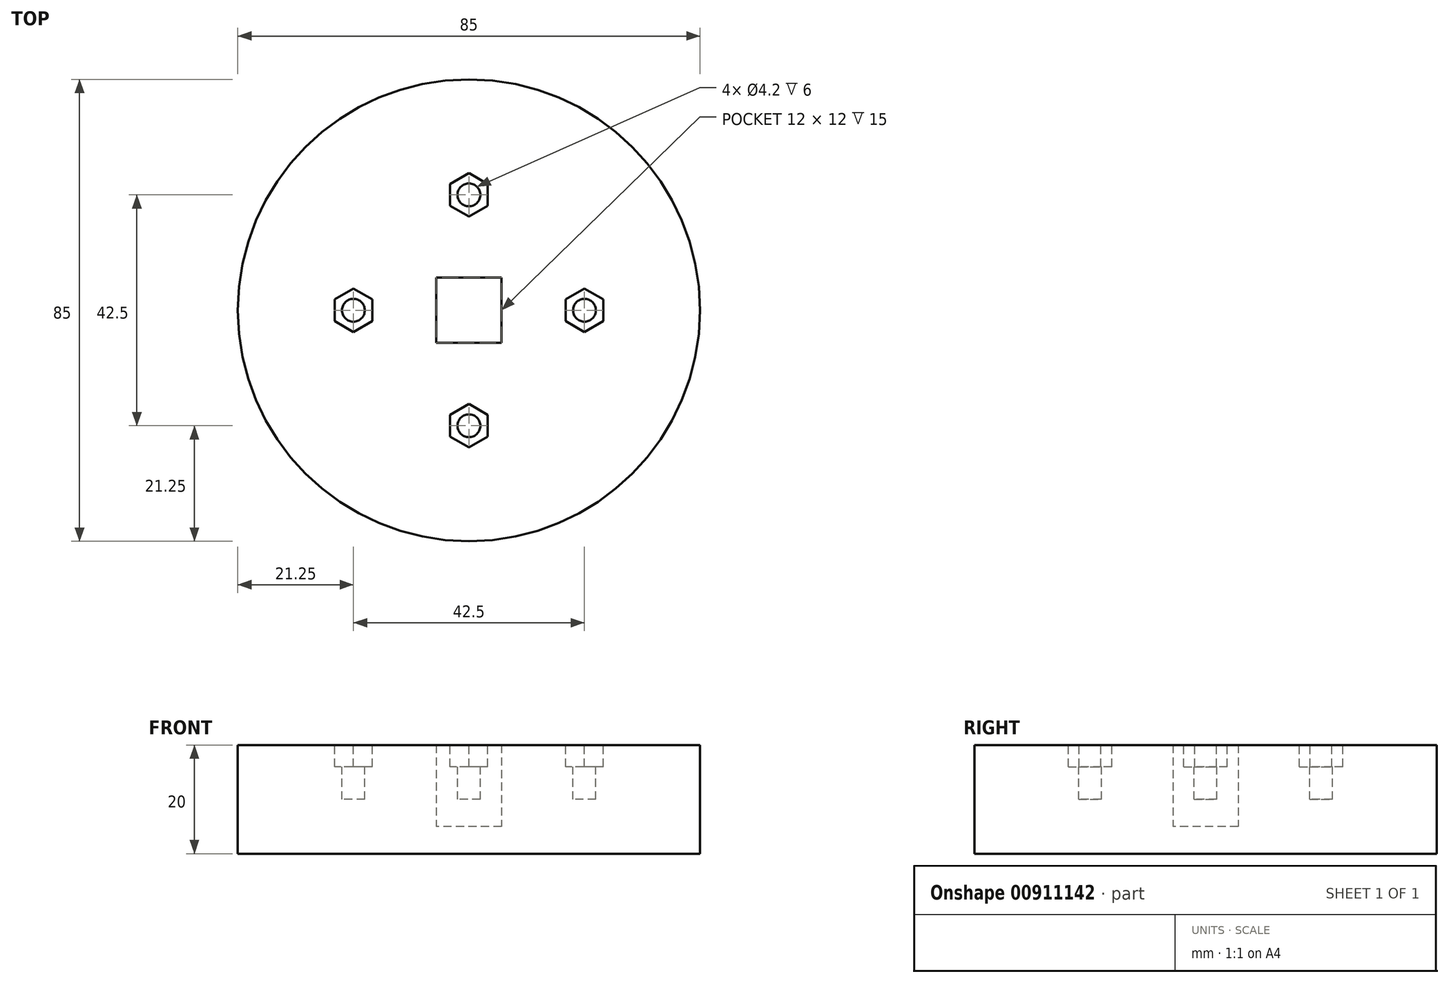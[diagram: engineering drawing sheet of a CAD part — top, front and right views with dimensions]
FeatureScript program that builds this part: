
annotation { "Feature Type Name" : "Feature", "Feature Type Description" : "" }
export const myFeature = defineFeature(function(context is Context, id is Id, definition is map)
    precondition{}
    {
        {
            var Q0;
            Q0=qCreatedBy(makeId("Top.planeOp"),FACE);
            var sketch = newSketch(context, id + "F0", { "sketchPlane" : qUnion([Q0])});
            skLineSegment(sketch, "E0.bottom", {"start": v(6, 6) * mm, "end": v(-6, 6) * mm});
            skLineSegment(sketch, "E0.top", {"start": v(6, -6) * mm, "end": v(-6, -6) * mm});
            skLineSegment(sketch, "E0.left", {"start": v(6, 6) * mm, "end": v(6, -6) * mm});
            skLineSegment(sketch, "E0.right", {"start": v(-6, 6) * mm, "end": v(-6, -6) * mm});
            skPoint(sketch, "E0.middle", {"position": v(0, 0) * mm});
            skCircle(sketch, "E1", {"center": v(0, 0) * mm, "radius": 42.5 * mm});
            skSolve(sketch);
        }
        {
            var Q0;
            Q0 = qSketchRegion(id + "F0", true);
            extrude(context, id + "F1", {"entities" : qUnion([Q0]), "depth" : 15 * mm, "offsetDistance" : 25 * mm});
        }
        {
            var Q0;
            Q0=makeQuery(id+"F1.opExtrude","CAP_FACE",FACE,{"disambiguationData":[OSD([sQuery(id+"F0.wireOp",EDGE,"E0.bottom"),sQuery(id+"F0.wireOp",EDGE,"E0.top"),sQuery(id+"F0.wireOp",EDGE,"E0.left"),sQuery(id+"F0.wireOp",EDGE,"E0.right"),sQuery(id+"F0.wireOp",EDGE,"E1")])],"isStart":true});
            var sketch = newSketch(context, id + "F2", { "sketchPlane" : qUnion([Q0])});
            skCircle(sketch, "E2", {"center": v(0, 0) * mm, "radius": 42.5 * mm});
            skSolve(sketch);
        }
        {
            var Q0;
            Q0 = qSketchRegion(id + "F2", true);
            extrude(context, id + "F3", {"entities" : qUnion([Q0]), "operationType" : NewBodyOperationType.ADD, "depth" : 5 * mm, "offsetDistance" : 25 * mm});
        }
        {
            var Q0;
            Q0=makeQuery(id+"F1.opExtrude","CAP_FACE",FACE,{"disambiguationData":[OSD([sQuery(id+"F0.wireOp",EDGE,"E0.bottom"),sQuery(id+"F0.wireOp",EDGE,"E0.top"),sQuery(id+"F0.wireOp",EDGE,"E0.left"),sQuery(id+"F0.wireOp",EDGE,"E0.right"),sQuery(id+"F0.wireOp",EDGE,"E1")])],"isStart":false});
            var sketch = newSketch(context, id + "F4", { "sketchPlane" : qUnion([Q0])});
            skCircle(sketch, "E3", {"center": v(0, 0) * mm, "radius": 21.25 * mm, "construction": true});
            skCircle(sketch, "E4", {"center": v(-21.25, 0) * mm, "radius": 2.1 * mm});
            skPoint(sketch, "E4.centerSnap0", {"position": v(-6, 0) * mm});
            skCircle(sketch, "E5", {"center": v(0, 21.25) * mm, "radius": 2.1 * mm});
            skCircle(sketch, "E6", {"center": v(21.25, 0) * mm, "radius": 2.1 * mm});
            skCircle(sketch, "E7", {"center": v(0, -21.25) * mm, "radius": 2.1 * mm});
            skPoint(sketch, "E7.centerSnap0", {"position": v(0, -6) * mm});
            skSolve(sketch);
        }
        {
            var Q0;
            Q0 = qSketchRegion(id + "F4", true);
            extrude(context, id + "F5", {"entities" : qUnion([Q0]), "operationType" : NewBodyOperationType.REMOVE, "oppositeDirection" : true, "depth" : 10 * mm, "offsetDistance" : 25 * mm});
        }
        {
            var Q0;
            Q0=makeQuery(id+"F1.opExtrude","CAP_FACE",FACE,{"disambiguationData":[OSD([sQuery(id+"F0.wireOp",EDGE,"E0.bottom"),sQuery(id+"F0.wireOp",EDGE,"E0.top"),sQuery(id+"F0.wireOp",EDGE,"E0.left"),sQuery(id+"F0.wireOp",EDGE,"E0.right"),sQuery(id+"F0.wireOp",EDGE,"E1")])],"isStart":false});
            var sketch = newSketch(context, id + "F6", { "sketchPlane" : qUnion([Q0])});
            skCircle(sketch, "E8.cCircle", {"center": v(-21.25, 0) * mm, "radius": 3.46 * mm, "construction": true});
            skLineSegment(sketch, "E8.0", {"start": v(-24.71, -2) * mm, "end": v(-24.71, 2) * mm});
            skLineSegment(sketch, "E8.1", {"start": v(-24.71, 2) * mm, "end": v(-21.25, 4) * mm});
            skLineSegment(sketch, "E8.2", {"start": v(-21.25, 4) * mm, "end": v(-17.79, 2) * mm});
            skLineSegment(sketch, "E8.3", {"start": v(-17.79, 2) * mm, "end": v(-17.79, -2) * mm});
            skLineSegment(sketch, "E8.4", {"start": v(-17.79, -2) * mm, "end": v(-21.25, -4) * mm});
            skLineSegment(sketch, "E8.5", {"start": v(-21.25, -4) * mm, "end": v(-24.71, -2) * mm});
            skPoint(sketch, "E8.0.midPoint", {"position": v(-24.71, 0) * mm});
            skCircle(sketch, "E9.cCircle", {"center": v(0, 21.25) * mm, "radius": 3.46 * mm, "construction": true});
            skLineSegment(sketch, "E9.0", {"start": v(-3.46, 19.25) * mm, "end": v(-3.46, 23.25) * mm});
            skLineSegment(sketch, "E9.1", {"start": v(-3.46, 23.25) * mm, "end": v(0, 25.25) * mm});
            skLineSegment(sketch, "E9.2", {"start": v(0, 25.25) * mm, "end": v(3.46, 23.25) * mm});
            skLineSegment(sketch, "E9.3", {"start": v(3.46, 23.25) * mm, "end": v(3.46, 19.25) * mm});
            skLineSegment(sketch, "E9.4", {"start": v(3.46, 19.25) * mm, "end": v(0, 17.25) * mm});
            skLineSegment(sketch, "E9.5", {"start": v(0, 17.25) * mm, "end": v(-3.46, 19.25) * mm});
            skPoint(sketch, "E9.0.midPoint", {"position": v(-3.46, 21.25) * mm});
            skCircle(sketch, "E10.cCircle", {"center": v(21.25, 0) * mm, "radius": 3.46 * mm, "construction": true});
            skLineSegment(sketch, "E10.0", {"start": v(17.79, -2) * mm, "end": v(17.79, 2) * mm});
            skLineSegment(sketch, "E10.1", {"start": v(17.79, 2) * mm, "end": v(21.25, 4) * mm});
            skLineSegment(sketch, "E10.2", {"start": v(21.25, 4) * mm, "end": v(24.71, 2) * mm});
            skLineSegment(sketch, "E10.3", {"start": v(24.71, 2) * mm, "end": v(24.71, -2) * mm});
            skLineSegment(sketch, "E10.4", {"start": v(24.71, -2) * mm, "end": v(21.25, -4) * mm});
            skLineSegment(sketch, "E10.5", {"start": v(21.25, -4) * mm, "end": v(17.79, -2) * mm});
            skPoint(sketch, "E10.0.midPoint", {"position": v(17.79, 0) * mm});
            skCircle(sketch, "E11.cCircle", {"center": v(0, -21.25) * mm, "radius": 3.46 * mm, "construction": true});
            skLineSegment(sketch, "E11.0", {"start": v(-3.46, -23.25) * mm, "end": v(-3.46, -19.25) * mm});
            skLineSegment(sketch, "E11.1", {"start": v(-3.46, -19.25) * mm, "end": v(0, -17.25) * mm});
            skLineSegment(sketch, "E11.2", {"start": v(0, -17.25) * mm, "end": v(3.46, -19.25) * mm});
            skLineSegment(sketch, "E11.3", {"start": v(3.46, -19.25) * mm, "end": v(3.46, -23.25) * mm});
            skLineSegment(sketch, "E11.4", {"start": v(3.46, -23.25) * mm, "end": v(0, -25.25) * mm});
            skLineSegment(sketch, "E11.5", {"start": v(0, -25.25) * mm, "end": v(-3.46, -23.25) * mm});
            skPoint(sketch, "E11.0.midPoint", {"position": v(-3.46, -21.25) * mm});
            skSolve(sketch);
        }
        {
            var Q0;
            Q0 = qSketchRegion(id + "F6", true);
            extrude(context, id + "F7", {"entities" : qUnion([Q0]), "operationType" : NewBodyOperationType.REMOVE, "oppositeDirection" : true, "depth" : 4 * mm, "offsetDistance" : 25 * mm});
        }
    });
